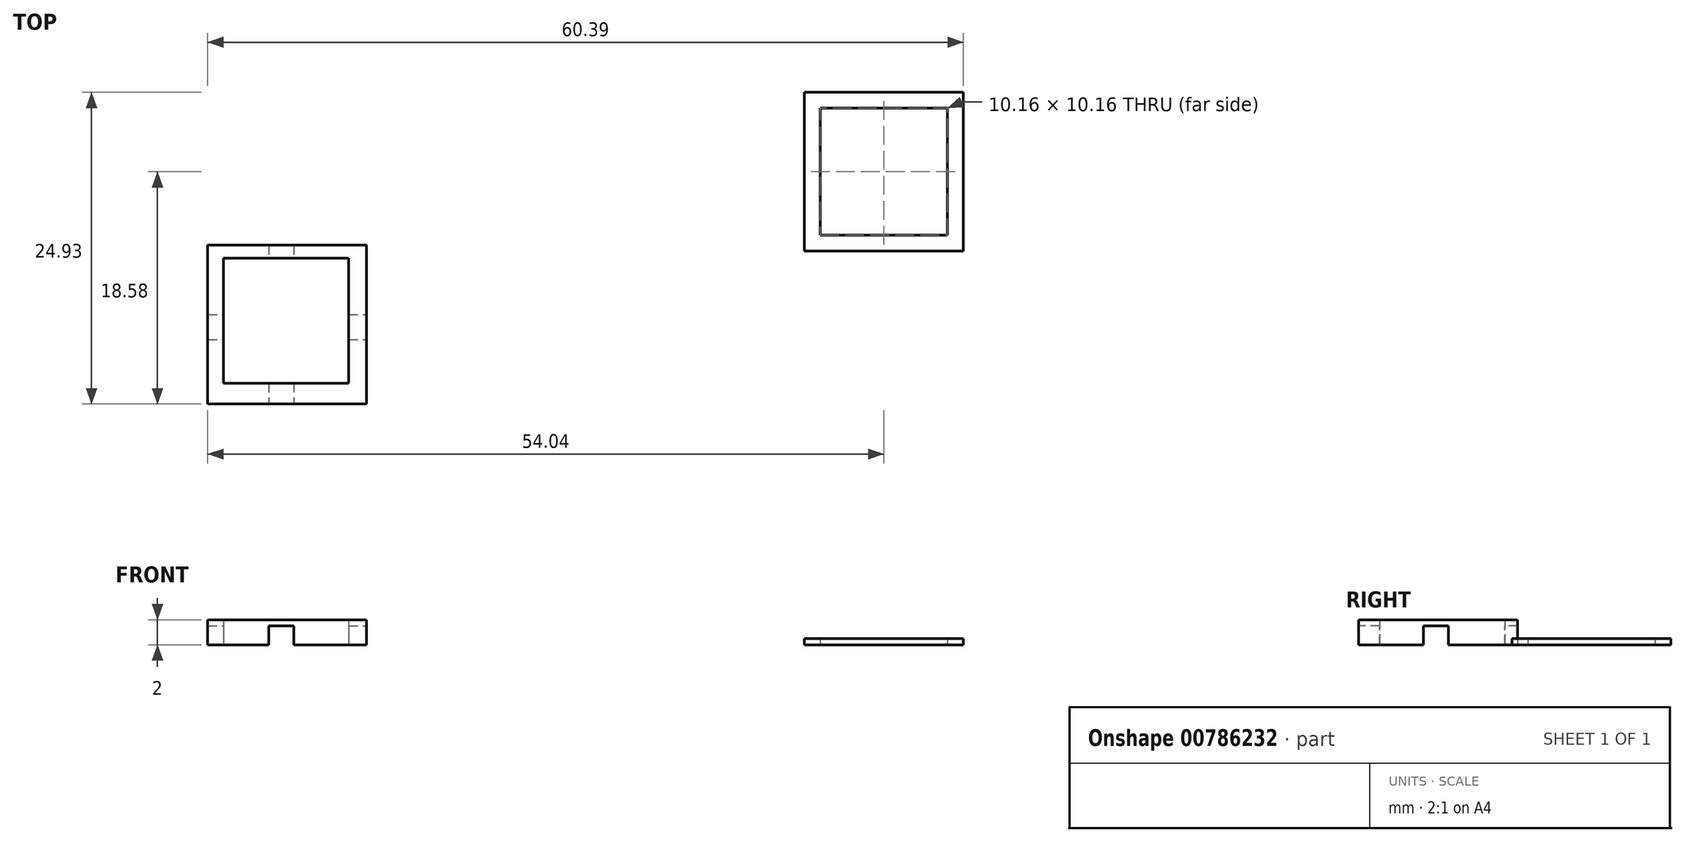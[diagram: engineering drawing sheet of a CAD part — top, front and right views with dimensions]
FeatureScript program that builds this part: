
annotation { "Feature Type Name" : "Feature", "Feature Type Description" : "" }
export const myFeature = defineFeature(function(context is Context, id is Id, definition is map)
    precondition{}
    {
        {
            var Q0;
            Q0=qCreatedBy(makeId("Top.planeOp"),FACE);
            var sketch = newSketch(context, id + "F0", { "sketchPlane" : qUnion([Q0])});
            skLineSegment(sketch, "E0.bottom", {"start": v(-6.35, 6.35) * mm, "end": v(6.35, 6.35) * mm});
            skLineSegment(sketch, "E0.top", {"start": v(-6.35, -6.35) * mm, "end": v(6.35, -6.35) * mm});
            skLineSegment(sketch, "E0.left", {"start": v(-6.35, 6.35) * mm, "end": v(-6.35, -6.35) * mm});
            skLineSegment(sketch, "E0.right", {"start": v(6.35, 6.35) * mm, "end": v(6.35, -6.35) * mm});
            skLineSegment(sketch, "E1.0", {"start": v(-5.08, 5.08) * mm, "end": v(-5.08, -5.08) * mm});
            skLineSegment(sketch, "E1.1", {"start": v(-5.08, 5.08) * mm, "end": v(5.08, 5.08) * mm});
            skLineSegment(sketch, "E1.2", {"start": v(5.08, 5.08) * mm, "end": v(5.08, -5.08) * mm});
            skLineSegment(sketch, "E1.3", {"start": v(-5.08, -5.08) * mm, "end": v(5.08, -5.08) * mm});
            skSolve(sketch);
        }
        {
            var Q0;
            Q0=makeQuery(id+"F0.imprint","IMPRINT",FACE,{"disambiguationData":[TD([[makeQuery(id+"F0.imprint","IMPRINT",EDGE,{"derivedFrom":sQuery(id+"F0.wireOp",EDGE,"E0.bottom")}),-1.0]])]});
            extrude(context, id + "F1", {"entities" : qUnion([Q0]), "depth" : 0.5 * mm, "offsetDistance" : 25.4 * mm});
        }
        {
            var Q0;
            Q0=qCreatedBy(makeId("Top.planeOp"),FACE);
            var sketch = newSketch(context, id + "F2", { "sketchPlane" : qUnion([Q0])});
            skLineSegment(sketch, "E2.bottom", {"start": v(-54.04, -5.88) * mm, "end": v(-41.34, -5.88) * mm});
            skLineSegment(sketch, "E2.top", {"start": v(-54.04, -18.58) * mm, "end": v(-41.34, -18.58) * mm});
            skLineSegment(sketch, "E2.left", {"start": v(-54.04, -5.88) * mm, "end": v(-54.04, -18.58) * mm});
            skLineSegment(sketch, "E2.right", {"start": v(-41.34, -5.88) * mm, "end": v(-41.34, -18.58) * mm});
            skLineSegment(sketch, "E3.bottom", {"start": v(-42.78, -16.9) * mm, "end": v(-52.78, -16.9) * mm});
            skLineSegment(sketch, "E3.top", {"start": v(-42.78, -6.9) * mm, "end": v(-52.78, -6.9) * mm});
            skLineSegment(sketch, "E3.left", {"start": v(-42.78, -16.9) * mm, "end": v(-42.78, -6.9) * mm});
            skLineSegment(sketch, "E3.right", {"start": v(-52.78, -16.9) * mm, "end": v(-52.78, -6.9) * mm});
            skPoint(sketch, "E3.middle", {"position": v(-47.78, -11.9) * mm});
            skSolve(sketch);
        }
        {
            var Q0;
            Q0=makeQuery(id+"F2.imprint","IMPRINT",FACE,{"disambiguationData":[TD([[makeQuery(id+"F2.imprint","IMPRINT",EDGE,{"derivedFrom":sQuery(id+"F2.wireOp",EDGE,"E2.bottom")}),-1.0]])]});
            extrude(context, id + "F3", {"entities" : qUnion([Q0]), "depth" : 2 * mm, "offsetDistance" : 25 * mm});
        }
        {
            var Q0;
            Q0=makeQuery(id+"F3.opExtrude","SWEPT_FACE",FACE,{"disambiguationData":[OSD([sQuery(id+"F2.wireOp",EDGE,"E2.right")])]});
            var sketch = newSketch(context, id + "F4", { "sketchPlane" : qUnion([Q0])});
            skLineSegment(sketch, "E4.bottom", {"start": v(-13.43, 0) * mm, "end": v(-11.43, 0) * mm});
            skLineSegment(sketch, "E4.top", {"start": v(-13.43, 1.5) * mm, "end": v(-11.43, 1.5) * mm});
            skLineSegment(sketch, "E4.left", {"start": v(-13.43, 0) * mm, "end": v(-13.43, 1.5) * mm});
            skLineSegment(sketch, "E4.right", {"start": v(-11.43, 0) * mm, "end": v(-11.43, 1.5) * mm});
            skSolve(sketch);
        }
        {
            var Q0;
            Q0=makeQuery(id+"F4.imprint","IMPRINT",FACE,{"disambiguationData":[TD([[makeQuery(id+"F4.imprint","IMPRINT",EDGE,{"derivedFrom":sQuery(id+"F4.wireOp",EDGE,"E4.bottom")}),-1.0]])]});
            extrude(context, id + "F5", {"entities" : qUnion([Q0]), "operationType" : NewBodyOperationType.REMOVE, "oppositeDirection" : true, "depth" : 25 * mm, "offsetDistance" : 25 * mm});
        }
        {
            var Q0;
            Q0=makeQuery(id+"F3.opExtrude","SWEPT_FACE",FACE,{"disambiguationData":[OSD([sQuery(id+"F2.wireOp",EDGE,"E2.top")])]});
            var sketch = newSketch(context, id + "F6", { "sketchPlane" : qUnion([Q0])});
            skLineSegment(sketch, "E5.bottom", {"start": v(-49.15, 0) * mm, "end": v(-47.15, 0) * mm});
            skLineSegment(sketch, "E5.top", {"start": v(-49.15, 1.5) * mm, "end": v(-47.15, 1.5) * mm});
            skLineSegment(sketch, "E5.left", {"start": v(-49.15, 0) * mm, "end": v(-49.15, 1.5) * mm});
            skLineSegment(sketch, "E5.right", {"start": v(-47.15, 0) * mm, "end": v(-47.15, 1.5) * mm});
            skSolve(sketch);
        }
        {
            var Q0;
            Q0=makeQuery(id+"F6.imprint","IMPRINT",FACE,{"disambiguationData":[TD([[makeQuery(id+"F6.imprint","IMPRINT",EDGE,{"derivedFrom":sQuery(id+"F6.wireOp",EDGE,"E5.bottom")}),1.0]])]});
            extrude(context, id + "F7", {"entities" : qUnion([Q0]), "operationType" : NewBodyOperationType.REMOVE, "oppositeDirection" : true, "depth" : 25 * mm, "offsetDistance" : 25 * mm});
        }
    });
